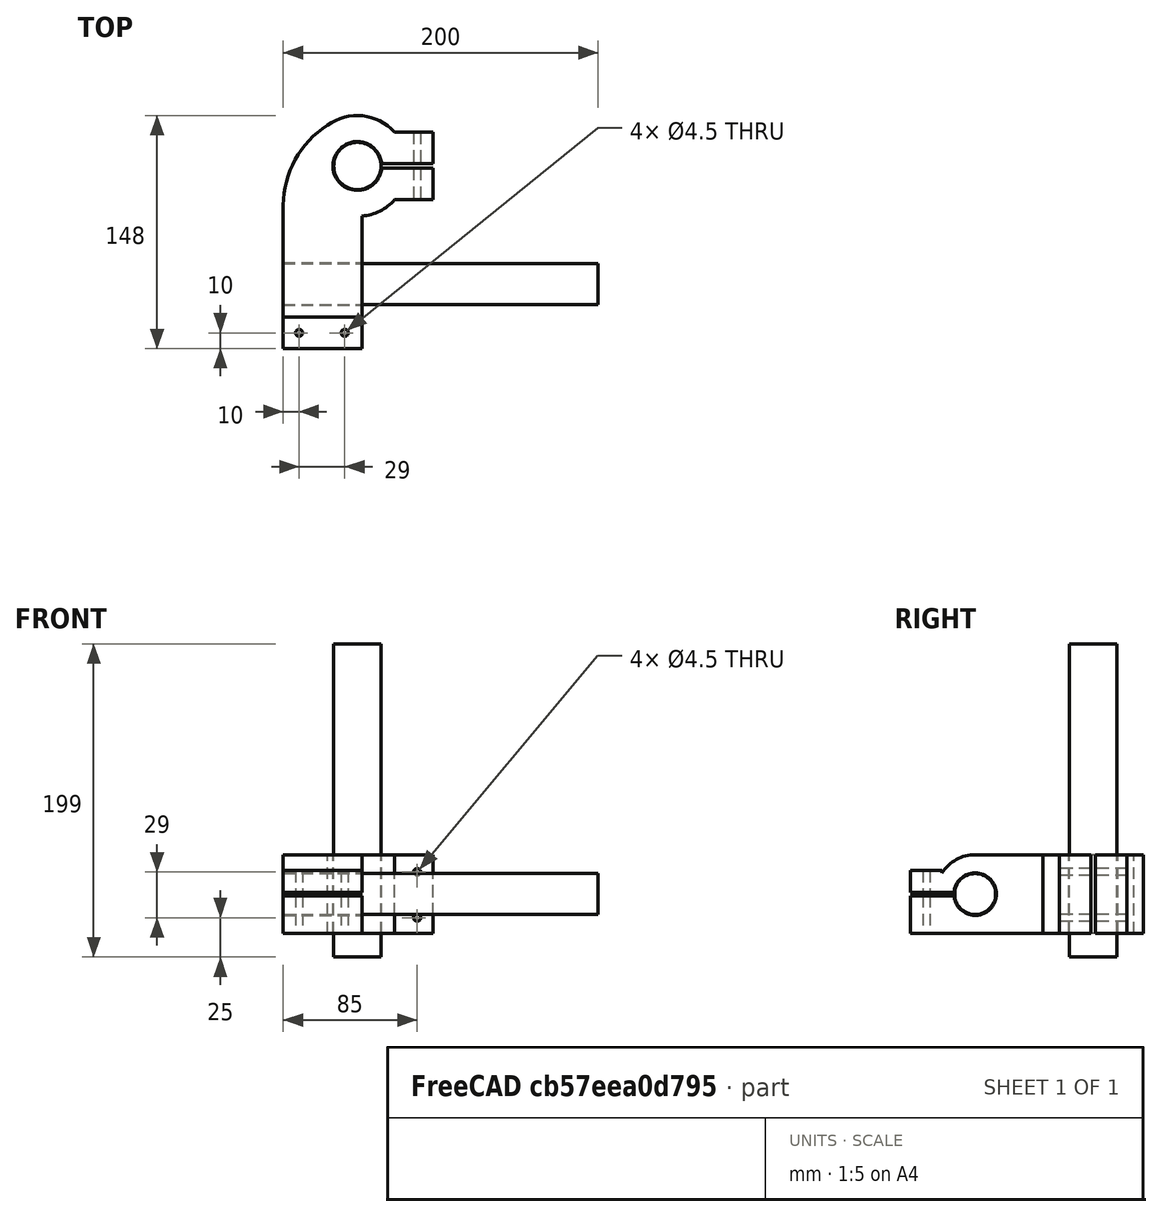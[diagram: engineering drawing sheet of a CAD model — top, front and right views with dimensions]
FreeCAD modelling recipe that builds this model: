
FCSTD DOCUMENT  (FreeCAD 0.19R24267 +99 (Git))
Label: camMountBAck2022_02_26
License: All rights reserved
LicenseURL: http://en.wikipedia.org/wiki/All_rights_reserved
objects: Part::Cylinder×9, Part::Box×8, Part::MultiFuse×4, Part::FeaturePython×2, Part::Cut×1
note: 24 computed .brp shape members not serialized (recipe doc carries the construction recipe); baked Part::Feature solids carry a one-line shape summary decoded from their .brp

FEATURE [Part::Cylinder] Cylinder  label="Horizontal"
  Angle = 360
  AttacherType = Attacher::AttachEngine3D
  Height = 199
  Radius = 15
FEATURE [Part::Cylinder] Cylinder001  label="Vertical"
  Angle = 360
  AttacherType = Attacher::AttachEngine3D
  Height = 200
  Placement = pos=(-47,-75,40) rot=(0.57735,0.57735,0.57735;2.0944rad)
  Radius = 13
FEATURE [Part::FeaturePython] Tube  label="TubeAddons"  # WARN: FeaturePython — macro-defined, semantics opaque (R4)
  AttacherType = Attacher::AttachEngine3D
  Height = 50
  InnerRadius = 15.5
  OuterRadius = 32
  Placement = pos=(0,0,15) rot=(0,0,1;0rad)
FEATURE [Part::FeaturePython] Tube001  label="TubeAddons001"  # WARN: FeaturePython — macro-defined, semantics opaque (R4)
  AttacherType = Attacher::AttachEngine3D
  Height = 50
  InnerRadius = 13.5
  OuterRadius = 25
  Placement = pos=(-47,-75,40) rot=(0,1,0;1.5708rad)
FEATURE [Part::Box] Box  label="horCuts"
  AttacherType = Attacher::AttachEngine3D
  Height = 50
  Length = 20
  Placement = pos=(14,-1.5,15) rot=(0,0,1;0rad)
  Width = 3
FEATURE [Part::Box] Box001  label="horAdd"
  AttacherType = Attacher::AttachEngine3D
  Height = 50
  Length = 25
  Placement = pos=(23,-21.5,15) rot=(0,0,1;0rad)
  Width = 20
FEATURE [Part::Box] Box002  label="horAdd001"
  AttacherType = Attacher::AttachEngine3D
  Height = 50
  Length = 25
  Placement = pos=(23,1.5,15) rot=(0,0,1;0rad)
  Width = 20
FEATURE [Part::Box] Box003  label="VerAddons"
  AttacherType = Attacher::AttachEngine3D
  Height = 10
  Length = 50
  Placement = pos=(-47,-116,15) rot=(0,0,1;0rad)
  Width = 75
FEATURE [Part::Box] Box004  label="VerAddons001"
  AttacherType = Attacher::AttachEngine3D
  Height = 14
  Length = 50
  Placement = pos=(-47,-116,25) rot=(0,0,1;0rad)
  Width = 52
FEATURE [Part::Box] Box005  label="VerAddons002"
  AttacherType = Attacher::AttachEngine3D
  Height = 14
  Length = 50
  Placement = pos=(-47,-116,41) rot=(0,0,1;0rad)
  Width = 20
FEATURE [Part::Box] Box006  label="verCuts"
  AttacherType = Attacher::AttachEngine3D
  Height = 2
  Length = 50
  Placement = pos=(-47,-110,39) rot=(0,0,1;0rad)
  Width = 27
FEATURE [Part::Cylinder] Cylinder002  label="AddCylinder"
  Angle = 60
  AttacherType = Attacher::AttachEngine3D
  Height = 50
  Placement = pos=(13,-25,15) rot=(0,0,1;2.0944rad)
  Radius = 60
FEATURE [Part::Box] Box007  label="VerAddons003"
  AttacherType = Attacher::AttachEngine3D
  Height = 50
  Length = 50
  Placement = pos=(-47,-75,15) rot=(0,0,1;0rad)
  Width = 50
FEATURE [Part::Cylinder] Cylinder003  label="Vertical001Cuts"
  Angle = 360
  AttacherType = Attacher::AttachEngine3D
  Height = 200
  Placement = pos=(-47,-75,40) rot=(0.57735,0.57735,0.57735;2.0944rad)
  Radius = 13.5
FEATURE [Part::Cylinder] Cylinder004  label="Horizontal001Cuts"
  Angle = 360
  AttacherType = Attacher::AttachEngine3D
  Height = 199
  Radius = 15.5
FEATURE [Part::Cylinder] Cylinder005  label="m4s"
  Angle = 360
  AttacherType = Attacher::AttachEngine3D
  Height = 50
  Placement = pos=(38,22,25) rot=(1,0,0;1.5708rad)
  Radius = 2.25
FEATURE [Part::Cylinder] Cylinder006  label="m4s001"
  Angle = 360
  AttacherType = Attacher::AttachEngine3D
  Height = 50
  Placement = pos=(38,22,54) rot=(1,0,0;1.5708rad)
  Radius = 2.25
FEATURE [Part::MultiFuse] Fusion  label="m4s002"
  Placement = pos=(-62,-144,43) rot=(0.57735,0.57735,0.57735;2.0944rad)
  Shapes = -> [Cylinder006,Cylinder005]
FEATURE [Part::Cylinder] Cylinder007  label="m4s004"
  Angle = 360
  AttacherType = Attacher::AttachEngine3D
  Height = 50
  Placement = pos=(38,22,25) rot=(1,0,0;1.5708rad)
  Radius = 2.25
FEATURE [Part::Cylinder] Cylinder008  label="m4s005"
  Angle = 360
  AttacherType = Attacher::AttachEngine3D
  Height = 50
  Placement = pos=(38,22,54) rot=(1,0,0;1.5708rad)
  Radius = 2.25
FEATURE [Part::MultiFuse] Fusion001  label="m4s003"
  Shapes = -> [Cylinder008,Cylinder007]
FEATURE [Part::MultiFuse] Fusion002  label="cuts"
  Shapes = -> [Fusion001,Fusion,Cylinder004,Cylinder003,Box,Box006]
FEATURE [Part::MultiFuse] Fusion003  label="addons"
  Shapes = -> [Box007,Box001,Box002,Box003,Box004,Box005,Cylinder002,Tube,Tube001]
FEATURE [Part::Cut] Cut  label="rear"
  Base = -> Fusion003
  Tool = -> Fusion002
